# Revit family: QF_MACOM_MVT1GC_70xxxP
name_source: partatom
category: Equipamento especial
units: mm (PartAtom-declared; Revit-internal decimal feet)

## family parameters
Com base no plano de trabalho = Não
Compartilhado = Não
Corte com vazios quando carregada = Não
Cota do conector redondo = Utilizar diâmetro
Número OmniClass = 23.40.40.14
Ponto de cálculo do ambiente = Não
Sempre na vertical = Sim
Tipo de parte = Normal
Título OmniClass = Food Service Equipment

## types (5) — shared parameters
Elevação padrão = 0 mm
Fabricante = MACOM
URL = https://www.acosmacom.com.br
Valve Size = 3 1/2"

## per-type parameters (varying)
| type | Descrição | Foot w/ + 2000 | Length Actual |
| MVT1GC-70250P | MESA VINCADA INOX PREMIUM MACOM ESP.TRASEIRO + 1 CUBA CENTRAL 705040 - 2500X700X900mm | Sim | 2500 mm |
| MVT1GC-70200P | MESA VINCADA INOX PREMIUM MACOM ESP.TRASEIRO + 1 CUBA CENTRAL 705040 - 2000X700X900mm | Não | 2000 mm |
| MVT1GC-70180P | MESA VINCADA INOX PREMIUM MACOM ESP.TRASEIRO + 1 CUBA CENTRAL 625030 - 1800X700X900mm
MESA LISA INOX PREMIUM MACOM CENTRO 700X700X900mm
MESA VINCADA INOX PREMIUM MACOM ESP.TRASEIRO + 1 CUBA CENTRAL 705040 - 1800x700X900mm | Não | 1800 mm |
| MVT1GC-70140P | MESA VINCADA INOX PREMIUM MACOM ESP.TRASEIRO + 1 CUBA CENTRAL 705040 - 1400X700X900mm | Não | 1400 mm |
| MVT1GC-7080P | MESA VINCADA INOX PREMIUM MACOM ESP.TRASEIRO + 1 CUBA CENTRAL 705040 - 800X700X900mm | Não | 800 mm |

note: column(s) folded — value = type name in every type: Modelo

## geometry (parser evidence)
native form markers: Sweep x3
no freeform markers — native parametric forms only
